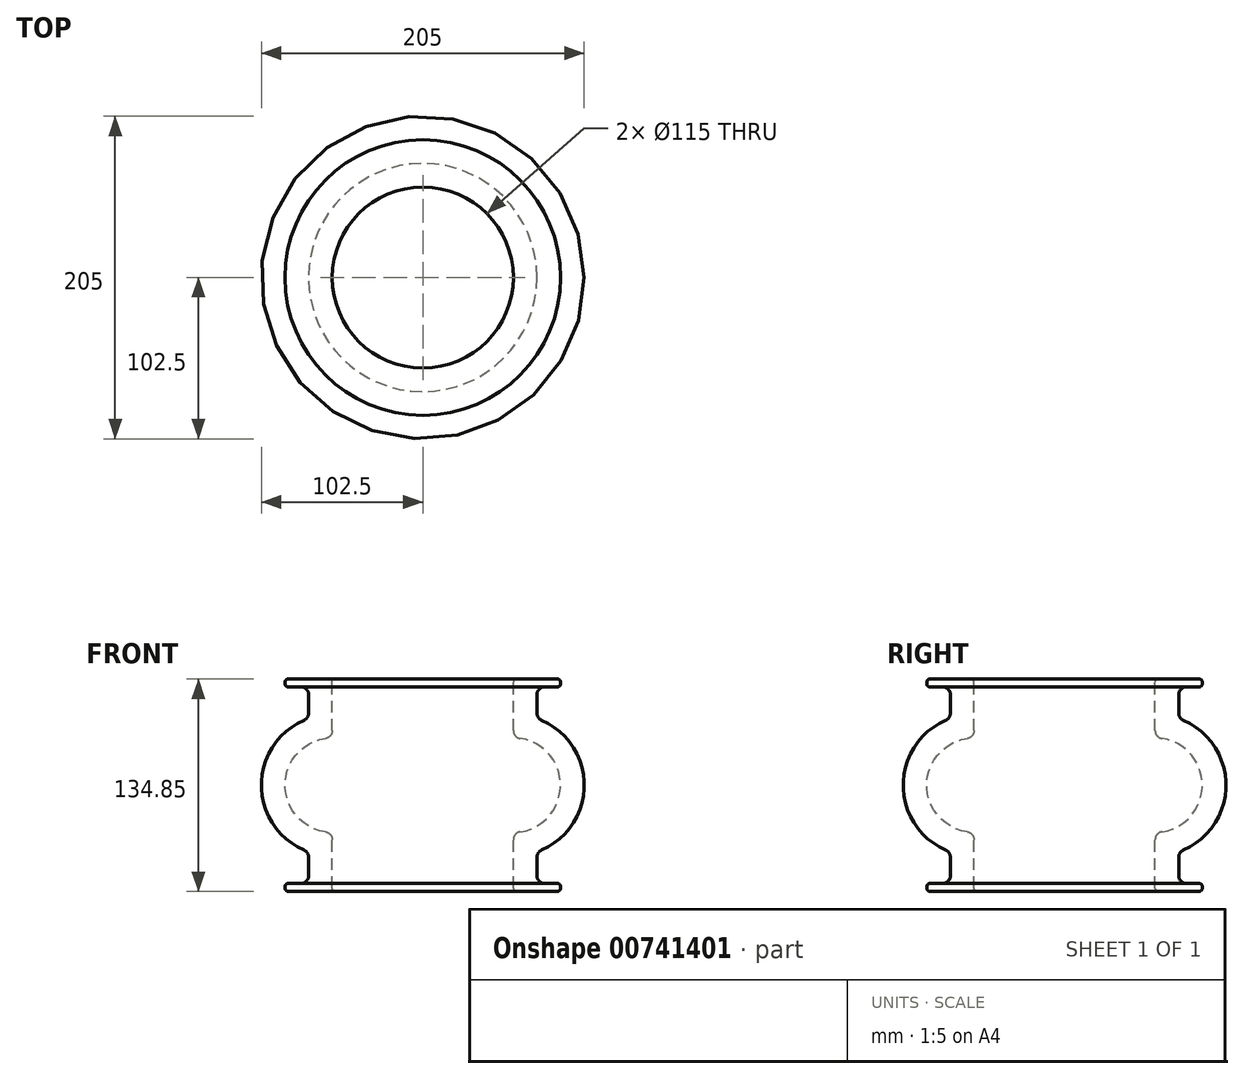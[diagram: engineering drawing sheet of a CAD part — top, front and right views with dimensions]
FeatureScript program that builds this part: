
annotation { "Feature Type Name" : "Feature", "Feature Type Description" : "" }
export const myFeature = defineFeature(function(context is Context, id is Id, definition is map)
    precondition{}
    {
        {
            var Q0;
            Q0=qCreatedBy(makeId("Right.planeOp"),FACE);
            var sketch = newSketch(context, id + "F0", { "sketchPlane" : qUnion([Q0])});
            skLineSegment(sketch, "E0", {"start": v(0, 75.5) * mm, "end": v(0, -68.38) * mm, "construction": true});
            skLineSegment(sketch, "E1", {"start": v(-59.5, 0) * mm, "end": v(-85.5, 0) * mm});
            skLineSegment(sketch, "E2", {"start": v(-87.5, 2) * mm, "end": v(-87.5, 3) * mm});
            skLineSegment(sketch, "E3", {"start": v(-85.5, 5) * mm, "end": v(-77.5, 5) * mm});
            skLineSegment(sketch, "E4", {"start": v(-72.5, 10) * mm, "end": v(-72.5, 21.6) * mm});
            skArc(sketch, "E5", {"start": v(-75.5, 108.67) * mm, "mid": v(-102.5, 67.43) * mm, "end": v(-75.5, 26.18) * mm});
            skLineSegment(sketch, "E6", {"start": v(-143.64, 67.43) * mm, "end": v(-41.14, 67.43) * mm, "construction": true});
            skLineSegment(sketch, "E7.MirrorCS", {"start": v(-72.5, 124.85) * mm, "end": v(-72.5, 113.25) * mm});
            skLineSegment(sketch, "E8.MirrorCS", {"start": v(-85.5, 129.85) * mm, "end": v(-77.5, 129.85) * mm});
            skLineSegment(sketch, "E9.MirrorCS", {"start": v(-87.5, 132.85) * mm, "end": v(-87.5, 131.85) * mm});
            skLineSegment(sketch, "E10.MirrorCS", {"start": v(-59.5, 134.85) * mm, "end": v(-85.5, 134.85) * mm});
            skArc(sketch, "E11", {"start": v(-61.79, 97.12) * mm, "mid": v(-87.5, 67.43) * mm, "end": v(-61.79, 37.73) * mm});
            skLineSegment(sketch, "E12", {"start": v(-57.5, 102.07) * mm, "end": v(-57.5, 132.85) * mm});
            skLineSegment(sketch, "E13", {"start": v(-57.5, 32.79) * mm, "end": v(-57.5, 2) * mm});
            skPoint(sketch, "E14.visualSharp", {"position": v(-72.5, 109.85) * mm});
            skArc(sketch, "E14.filletArc", {"start": v(-75.5, 108.67) * mm, "mid": v(-73.32, 110.51) * mm, "end": v(-72.5, 113.25) * mm});
            skPoint(sketch, "E15.visualSharp", {"position": v(-72.5, 25) * mm});
            skArc(sketch, "E15.filletArc", {"start": v(-72.5, 21.6) * mm, "mid": v(-73.32, 24.34) * mm, "end": v(-75.5, 26.18) * mm});
            skPoint(sketch, "E16.visualSharp", {"position": v(-72.5, 5) * mm});
            skArc(sketch, "E16.filletArc", {"start": v(-77.5, 5) * mm, "mid": v(-73.96, 6.46) * mm, "end": v(-72.5, 10) * mm});
            skPoint(sketch, "E17.visualSharp", {"position": v(-57.5, 37.43) * mm});
            skArc(sketch, "E17.filletArc", {"start": v(-57.5, 32.79) * mm, "mid": v(-58.72, 36.06) * mm, "end": v(-61.79, 37.73) * mm});
            skPoint(sketch, "E18.visualSharp", {"position": v(-57.5, 97.43) * mm});
            skArc(sketch, "E18.filletArc", {"start": v(-61.79, 97.12) * mm, "mid": v(-58.72, 98.8) * mm, "end": v(-57.5, 102.07) * mm});
            skPoint(sketch, "E19.visualSharp", {"position": v(-72.5, 129.85) * mm});
            skArc(sketch, "E19.filletArc", {"start": v(-72.5, 124.85) * mm, "mid": v(-73.96, 128.39) * mm, "end": v(-77.5, 129.85) * mm});
            skPoint(sketch, "E20.visualSharp", {"position": v(-87.5, 134.85) * mm});
            skArc(sketch, "E20.filletArc", {"start": v(-85.5, 134.85) * mm, "mid": v(-86.91, 134.27) * mm, "end": v(-87.5, 132.85) * mm});
            skPoint(sketch, "E21.visualSharp", {"position": v(-87.5, 129.85) * mm});
            skArc(sketch, "E21.filletArc", {"start": v(-87.5, 131.85) * mm, "mid": v(-86.91, 130.44) * mm, "end": v(-85.5, 129.85) * mm});
            skPoint(sketch, "E22.visualSharp", {"position": v(-87.5, 5) * mm});
            skArc(sketch, "E22.filletArc", {"start": v(-85.5, 5) * mm, "mid": v(-86.91, 4.41) * mm, "end": v(-87.5, 3) * mm});
            skPoint(sketch, "E23.visualSharp", {"position": v(-87.5, 0) * mm});
            skArc(sketch, "E23.filletArc", {"start": v(-87.5, 2) * mm, "mid": v(-86.91, 0.59) * mm, "end": v(-85.5, 0) * mm});
            skPoint(sketch, "E24.visualSharp", {"position": v(-57.5, 0) * mm});
            skArc(sketch, "E24.filletArc", {"start": v(-59.5, 0) * mm, "mid": v(-58.09, 0.59) * mm, "end": v(-57.5, 2) * mm});
            skPoint(sketch, "E25.visualSharp", {"position": v(-57.5, 134.85) * mm});
            skArc(sketch, "E25.filletArc", {"start": v(-57.5, 132.85) * mm, "mid": v(-58.09, 134.27) * mm, "end": v(-59.5, 134.85) * mm});
            skSolve(sketch);
        }
        {
            var Q0;
            Q0=makeQuery(id+"F0.imprint","IMPRINT",FACE,{"disambiguationData":[TD([[makeQuery(id+"F0.imprint","IMPRINT",EDGE,{"derivedFrom":sQuery(id+"F0.wireOp",EDGE,"E1")}),-1.0]])]});
            var Q1;
            Q1=sQuery(id+"F0.wireOp",EDGE,"E0");
            revolve(context, id + "F1", {"surfaceOperationType" : NewSurfaceOperationType.NEW, "entities" : qUnion([Q0]), "axis" : qUnion([Q1]), "revolveType" : RevolveType.FULL});
        }
    });
